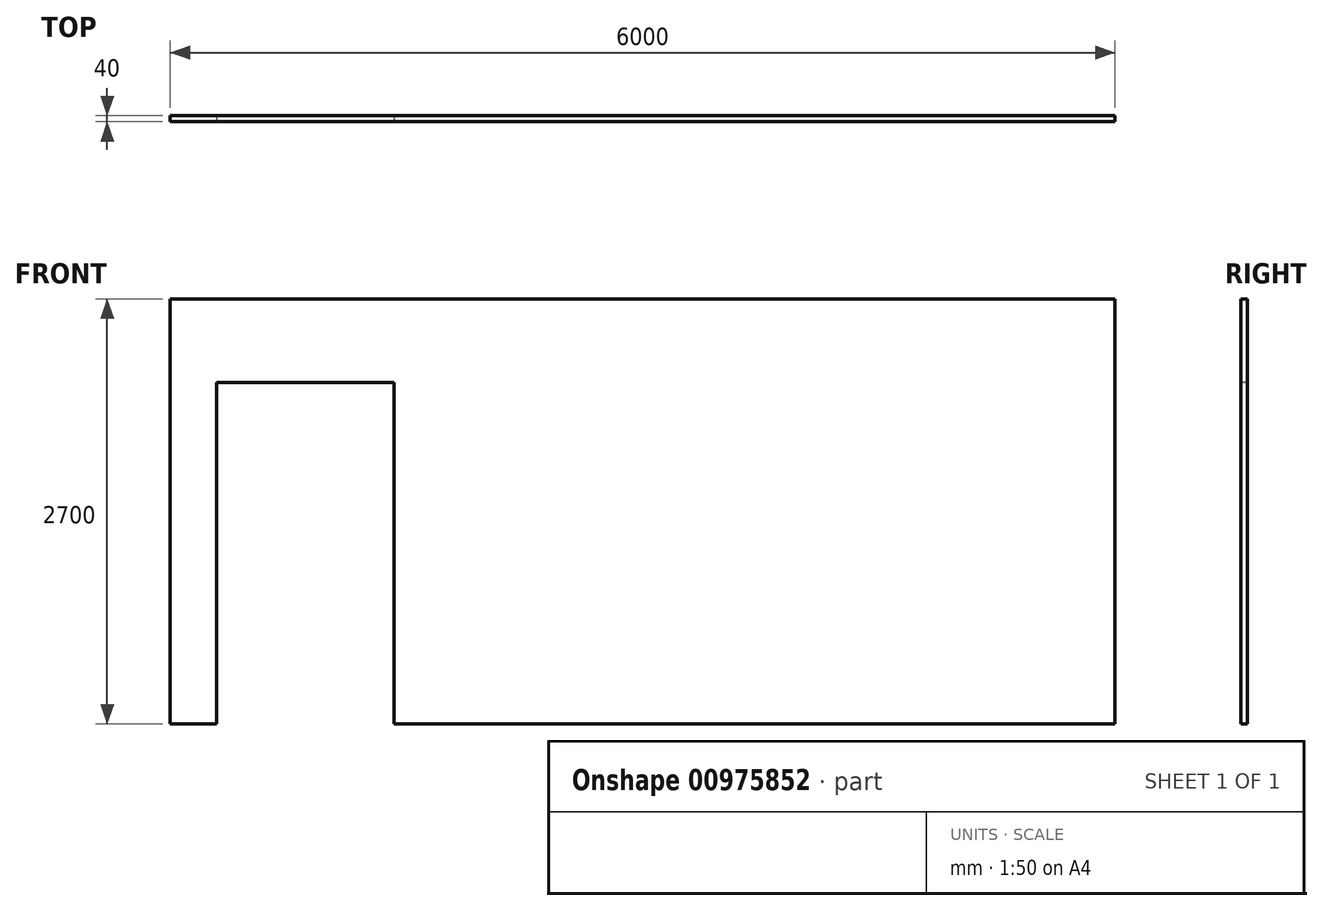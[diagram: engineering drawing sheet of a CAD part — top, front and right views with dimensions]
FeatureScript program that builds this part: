
annotation { "Feature Type Name" : "Feature", "Feature Type Description" : "" }
export const myFeature = defineFeature(function(context is Context, id is Id, definition is map)
    precondition{}
    {
        {
            var Q0;
            Q0=qCreatedBy(makeId("Front.planeOp"),FACE);
            var sketch = newSketch(context, id + "F0", { "sketchPlane" : qUnion([Q0])});
            skLineSegment(sketch, "E0.bottom", {"start": v(-3002.86, 1088) * mm, "end": v(2997.14, 1088) * mm});
            skLineSegment(sketch, "E0.top", {"start": v(-3002.86, -1612) * mm, "end": v(2997.14, -1612) * mm});
            skLineSegment(sketch, "E0.left", {"start": v(-3002.86, 1088) * mm, "end": v(-3002.86, -1612) * mm});
            skLineSegment(sketch, "E0.right", {"start": v(2997.14, 1088) * mm, "end": v(2997.14, -1612) * mm});
            skSolve(sketch);
        }
        {
            var Q0;
            Q0=makeQuery(id+"F0.imprint","IMPRINT",FACE,{"disambiguationData":[TD([[makeQuery(id+"F0.imprint","IMPRINT",EDGE,{"derivedFrom":sQuery(id+"F0.wireOp",EDGE,"E0.bottom")}),-1.0]])]});
            extrude(context, id + "F1", {"entities" : qUnion([Q0]), "depth" : 40 * mm, "offsetDistance" : 25 * mm});
        }
        {
            var Q0;
            Q0=makeQuery(id+"F1.opExtrude","CAP_FACE",FACE,{"disambiguationData":[OSD([sQuery(id+"F0.wireOp",EDGE,"E0.bottom"),sQuery(id+"F0.wireOp",EDGE,"E0.top"),sQuery(id+"F0.wireOp",EDGE,"E0.left"),sQuery(id+"F0.wireOp",EDGE,"E0.right")])],"isStart":false});
            var sketch = newSketch(context, id + "F2", { "sketchPlane" : qUnion([Q0])});
            skLineSegment(sketch, "E1.bottom", {"start": v(-2710.65, -1612) * mm, "end": v(-1582.32, -1612) * mm});
            skLineSegment(sketch, "E1.top", {"start": v(-2710.65, 558.36) * mm, "end": v(-1582.32, 558.36) * mm});
            skLineSegment(sketch, "E1.left", {"start": v(-2710.65, -1612) * mm, "end": v(-2710.65, 558.36) * mm});
            skLineSegment(sketch, "E1.right", {"start": v(-1582.32, -1612) * mm, "end": v(-1582.32, 558.36) * mm});
            skSolve(sketch);
        }
        {
            var Q0;
            Q0=makeQuery(id+"F2.imprint","IMPRINT",FACE,{"disambiguationData":[TD([[makeQuery(id+"F2.imprint","IMPRINT",EDGE,{"derivedFrom":sQuery(id+"F2.wireOp",EDGE,"E1.bottom")}),1.0]])]});
            extrude(context, id + "F3", {"entities" : qUnion([Q0]), "operationType" : NewBodyOperationType.REMOVE, "endBound" : BoundingType.THROUGH_ALL, "oppositeDirection" : true, "depth" : 25 * mm, "offsetDistance" : 25 * mm});
        }
    });
